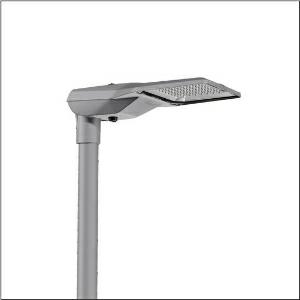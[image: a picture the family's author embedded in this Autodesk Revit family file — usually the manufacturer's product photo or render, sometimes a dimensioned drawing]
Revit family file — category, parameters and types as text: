
# Revit family: streetlight_sl_21_midi___pl52_5xe3h43t08mb_7d48
name_source: partatom
category: Lighting Fixtures
units: mm (PartAtom-declared; Revit-internal decimal feet)

## family parameters
Cut with Voids When Loaded = No
Host = Face
Light Source = No
Part Type = Normal
Room Calculation Point = No
Round Connector Dimension = Use Diameter
Shared = No

## types (1)
- --- (1 x LED, 19830 lm, 147 W, 4000K)
    Apparent Load = 147 VA
    CIE Flux Codes = 27 59 98 100 100
    Color Rendering = 70
    Color Temperature = 4000K
    Default Elevation = 1800 mm
    Description = Streetlight SL 21 midi, mast luminaire, primary light control with lens, of PMMA, primary optical cover: cover, of toughened safety glass, transparent, light distribution: PL52, light emission: direct distribution, primary light characteristic: asymmetric, installation type: side-entry, post-top, LED, High Power LED, rated luminous flux: 19.830lm, luminous efficacy: 135lm/W, light colour: 740, colour temperature: 4000K, control gear: D4i, control: overheat protection, constant luminous flux control, time-dependent luminous flux control, flexible luminous flux parameterisation, pre-setting: logarithmic dimming characteristic, mains connection: 230..240V, AC, 50/60Hz, start of lifetime: 147W, end of service life: 155W, reduction: 65W, luminaire housing, of diecast aluminium, powder-coated, SITECO metallic grey (DB 702S), corrosivity category C5 high according to DIN EN ISO 12944, please order mast flange separately, inclination adjustable: 0°, 5°, 10°, 15°, sealing non-destructively replaceable, multi-level sealing system, length: 644mm, width: 335mm, height: 110mm, mast flange for spigot size: 42mm (side-entry): 5XC10008XM4, 60/48mm (side-entry/post-top): 5XC10108XM2, 76/60mm (side-entry/post-top): 5XC10108XM1, mounting height: 4..8m, Smart Interface below and above, protection rating (complete): IP66, insulation class (complete): insulation class II (safety insulation), certification: CE, ENEC, ENEC+, VDE, impact resistance: IK10, permissible operating ambient temperature for outdoor applications: -40..+50°C, standard-compliant lighting for roads and squares, packaging unit: 1 piece

Light Distribution: PL52
    Height = 111 mm
    Lamp = 1 x LED
    Lamp Light Flux = 19830 lm
    Lamp Power = 147 W
    Lamp count = 1
    Length = 644 mm
    Luminous efficacy = 135 lm/W
    Manufacturer = Siteco
    ModVariant = No
    Model = 5XE3H43T08MB
    Number of Poles = 1
    OnlyDefault = Yes
    Power Factor = 1
    Product Name = Streetlight SL 21 midi | PL52
    Product group = mast luminaire | pylon top
    ProductGroupID = 6100
    Protection Class = Protection class II
    Protection Degree = IP 66
    RLX_Detail_Level = 1
    RLX_Emergency_Light_Flux = 0 lm
    RLX_Emergency_Type = 0
    RLX_Emergency_Type_DB = No
    RlxData = <blob elided: 36597 chars, md5=984d7299>
    Socket = socket
    Standby Power = 0 W
    System Light Flux = 19830 lm
    System Power = 147 W
    Type Comments = factory setting: luminous flux: 100 % | dim-lin: 254 | 750 mA
    Type Image = l_1004304.jpg
    URL = http://relux.com
    VarID = @adj_188015
    Voltage = 0 V
    Weight = 0.00 kg
    Width = 336 mm

## geometry (parser evidence)
native form markers: Blend x4, Sweep x9
no freeform markers — native parametric forms only
